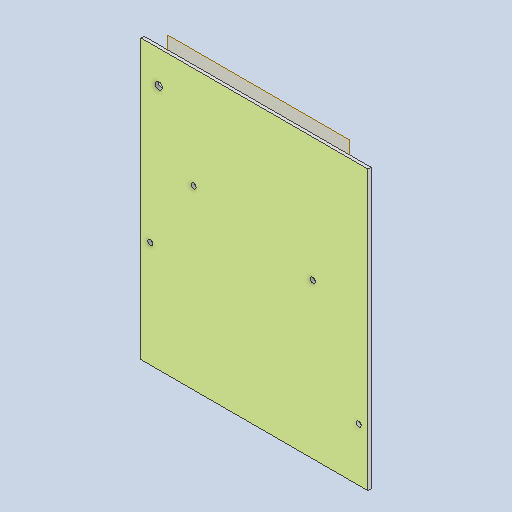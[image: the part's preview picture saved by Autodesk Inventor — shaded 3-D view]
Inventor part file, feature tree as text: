
AUTODESK INVENTOR PART (.ipt)
format: ipt  version: 2023.2 (Build 272271000, 271)  size: 141,824 bytes
history: native  units: mm
features: other x6, reference x6, hole x3, sketch x2, plane x1, extrude x1
ambient origin geometry x8: Origin, YZ Plane, XZ Plane, XY Plane, X Axis, Y Axis, Z Axis, Center Point
bodies: Body1 (feature_tree)
feature tree (19):
  other  "Z axis front plate"
  plane  "Work Plane1"
  extrude  "Extrusion1"  Depth=3.0mm
  hole  "Hole1"  [1 undecoded]
  hole  "Hole3"  [1 undecoded]
  hole  "Hole4"  [1 undecoded]
  reference  "Reference1"
  reference  "Reference2"
  sketch  "Sketch3"  dims[d1=3.0mm d2=0.0mm d4=33.0mm]
  reference  "Reference3"
  reference  "Reference4"
  reference  "Reference5"
  reference  "Reference6"
  sketch  "Sketch4"  dims[d5=5.1mm d6=6.0mm d7=4.0mm d8=2.0mm d9=90.0deg d10=8.0mm d11=20.594885mm d12=150.0mm d14=11.0mm d15=11.0mm d16=13.7mm d24=5.1mm d25=6.0mm d26=4.0mm d27=2.0mm d28=90.0deg d29=8.0mm d30=20.594885mm d31=7.1mm d32=6.0mm d33=4.0mm d34=2.0mm d35=90.0deg d36=8.0mm d37=20.594885mm d39=11.0mm d40=20.0mm d41=90.0deg d13=0.0625mm]
  parser-record x1  (decoder bookkeeping rows leaked as tree rows — omitted from the tree; the rows remain in map.json)
  other  "Main Assembly.iam"
  other  "Z axis Back Plate:1"
  other  "20x20-V-Slot-Extrusion:1"
  other  "20x20-V-Slot-Extrusion:2"
note: 3 required parameter values undecoded (feature->parameter linkage not recoverable at this tier; creation-order binding heuristic only, values carry confidence <= 0.55)
note: 1 file-system path scrubbed to <path> (originals preserved in map.json)
